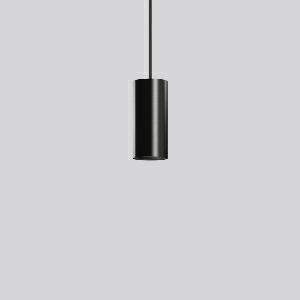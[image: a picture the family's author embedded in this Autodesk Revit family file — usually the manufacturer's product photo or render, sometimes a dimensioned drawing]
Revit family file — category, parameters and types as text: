
# Revit family: deecos_p_mini_911528_003_76_0e94
name_source: partatom
category: Lighting Fixtures
units: mm (PartAtom-declared; Revit-internal decimal feet)

## family parameters
Cut with Voids When Loaded = No
Host = Face
Light Source = No
Part Type = Normal
Room Calculation Point = No
Round Connector Dimension = Use Diameter
Shared = No

## types (1)
- DEECOS P mini (1 x LED Modul 930, 2750 lm, 3000)
    Apparent Load = 29 VA
    Approval mark = CE
    CIE Flux Codes = 95 100 100 100 100
    Color Rendering = 90
    Color Temperature = 3000
    Default Elevation = 1800 mm
    Description = Series: DEECOS P mini
Cylindrical pendant luminaire. Housing: die-cast aluminium, powder-coated. Canopy made of powder-coated sheet steel with magnetic attachment. Optical assembly with lens made of plastic (polycarbonate) for the best homogeneous light distribution - can be changed without tools. Oval light distribution for corridor. Best colour rendering index Ra>90. Transparent pendant cable 5 m, can be shortened, with integrated steel cable. High quality converter without flickering and stroboscopic effect. The following accessories can be mounted without use of tools: interchangeable lenses, honeycomb louvre, clear and frosted diffusers, white interchangeable plastic ring. Decorative recessed suspension set available as accessory.Suitable for accessory Deecos P Tube cylinder extensions 0.5 m, 0.75 m or 1 m. 
Colour: deep black, matt (RAL 9005)
Diameter: 87 mm
Height: 195 mm
Suspension length: 5000 mm
Lamp: LED
Socket: without socket
Colour temperature: 3000K
Colour rendering index (CRI): 92
System power: 29 W
Rated luminous flux: 2750 lm
Luminous efficiency: 95 lm/W
Control gear: Converter, dimmable, DALI
Protection class: I
Type of protection: IP 20
    Height = 195 mm
    Lamp = 1 x LED Modul 930
    Lamp Light Flux = 2750 lm
    Lamp count = 1
    Length = 87 mm
    Lifetime = 50000 h
    Luminous efficacy = 95 lm/W
    Manufacturer = RZB
    ModVariant = No
    Model = 911528.003.76
    Mounting Place = Ceiling
    Mounting Type = Pendant
    Number of Poles = 1
    OnlyDefault = Yes
    Power Factor = 1
    Product Name = DEECOS P mini
    Product group = Pendant luminaires
    ProductGroupID = 902
    Protection Class = Protection class I
    Protection Degree = IP 20
    RLX_Detail_Level = 1
    RLX_Emergency_Light_Flux = 0 lm
    RLX_Emergency_Type = 0
    RLX_Emergency_Type_DB = No
    RlxData = <blob elided: 64693 chars, md5=9b2ad882>
    Socket = socket
    Standby Power = 0 W
    System Light Flux = 2750 lm
    System Power = 29 W
    Type Comments = Product without accessories
    Type Image = 911476.003.jpg
    URL = http://relux.com
    VarID = ---
    Voltage = 230 V
    Voltage Range = 220-240 V
    Weight = 0.00 kg
    Width = 0 mm  [stored 0 ft]

note: [stored X ft] marks values corroborated as IEEE doubles in the binary element streams (Revit-internal decimal feet)

## geometry (parser evidence)
native form markers: Blend x4, Sweep x11
no freeform markers — native parametric forms only
